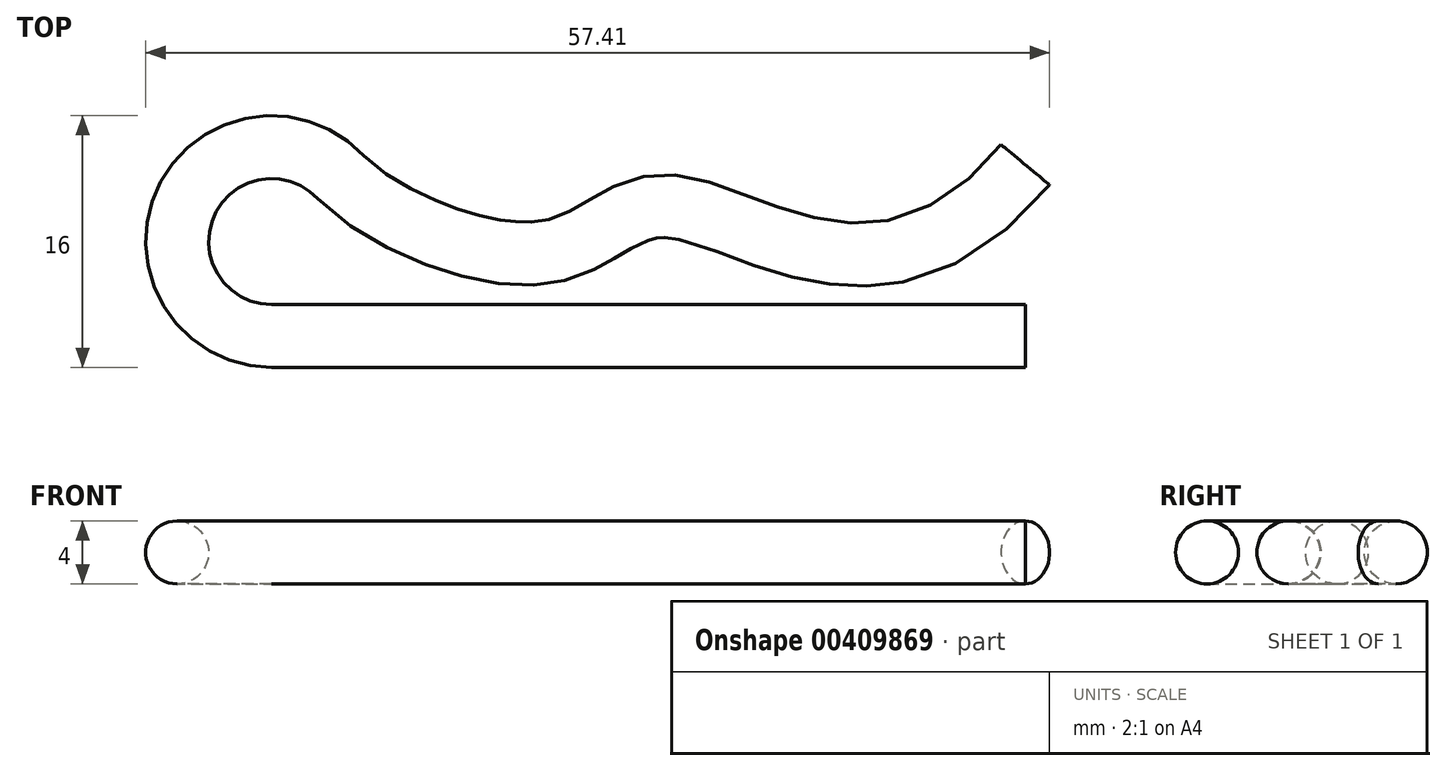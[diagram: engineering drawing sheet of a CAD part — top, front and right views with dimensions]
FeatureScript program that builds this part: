
annotation { "Feature Type Name" : "Feature", "Feature Type Description" : "" }
export const myFeature = defineFeature(function(context is Context, id is Id, definition is map)
    precondition{}
    {
        {
            var Q0;
            Q0=qCreatedBy(makeId("Top.planeOp"),FACE);
            var sketch = newSketch(context, id + "F0", { "sketchPlane" : qUnion([Q0])});
            skCircle(sketch, "E0", {"center": v(0, 0) * mm, "radius": 6 * mm, "construction": true});
            skLineSegment(sketch, "E1", {"start": v(22.64, 0) * mm, "end": v(-25.23, 0) * mm});
            skArc(sketch, "E2", {"start": v(-25.23, 0) * mm, "mid": v(-30.73, 8.4) * mm, "end": v(-20.85, 10.1) * mm});
            skFitSpline(sketch, "E3", {"points": [v(-20.85, 10.1) * mm, v(-7.72, 5.33) * mm, v(0, 8.25) * mm, v(22.64, 10.88) * mm], "startDerivative": vector(22.33, -23.93) * mm, "endDerivative": vector(64.47, 77.8) * mm});
            skSolve(sketch);
        }
        {
            var Q0;
            Q0=qCreatedBy(makeId("Right.planeOp"),FACE);
            var Q1;
            Q1=sQuery(id+"F0.wireOp",VERTEX,"E1.start");
            cPlane(context, id + "F1", {"entities" : qUnion([Q0, Q1]), "cplaneType" : CPlaneType.PLANE_POINT, "offset" : 25 * mm, "width" : 150 * mm, "height" : 150 * mm});
        }
        {
            var Q0;
            Q0=qCreatedBy(id+"F1.planeOp",FACE);
            var sketch = newSketch(context, id + "F2", { "sketchPlane" : qUnion([Q0])});
            skCircle(sketch, "E4", {"center": v(0, 0) * mm, "radius": 2 * mm});
            skSolve(sketch);
        }
        {
            var Q0;
            Q0=makeQuery(id+"F2.imprint","IMPRINT",FACE,{"disambiguationData":[TD([[makeQuery(id+"F2.imprint","IMPRINT",EDGE,{"derivedFrom":sQuery(id+"F2.wireOp",EDGE,"E4")}),1.0]])]});
            var Q1;
            Q1=sQuery(id+"F2.wireOp",EDGE,"E4");
            var Q2;
            Q2=qConstructionFilter(qBodyType(qCreatedBy(id+"F0",EDGE),BodyType.WIRE),ConstructionObject.NO);
            sweep(context, id + "F3", {"profiles" : qUnion([Q0]), "surfaceProfiles" : qUnion([Q1]), "path" : qUnion([Q2])});
        }
    });
